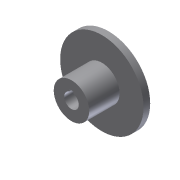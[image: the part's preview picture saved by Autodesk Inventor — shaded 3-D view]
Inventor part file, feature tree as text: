
AUTODESK INVENTOR PART (.ipt)
format: ipt  version: 2013 (Build 170138000, 138)  size: 94,208 bytes
history: native  units: in
note: dims shown in document units (in); Inventor stores cm internally (conversion verified against a paired STEP export)
features: extrude x3, sketch x3
ambient origin geometry x8: Origin, YZ Plane, XZ Plane, XY Plane, X Axis, Y Axis, Z Axis, Center Point
bodies: Solid1 (feature_tree)
feature tree (6):
  extrude  "Extrusion1"  Depth=0.18in TaperAngle=0.0deg
  extrude  "Extrusion2"  Depth=0.82in TaperAngle=0.0deg
  extrude  "Extrusion3"  Depth=0.0984in
  sketch  "Sketch1"  dims[d0=2.25in d1=0.18in d2=0.0in]
  sketch  "Sketch2"  dims[d3=0.958in d4=0.82in d5=0.0in]
  sketch  "Sketch3"  dims[d6=0.3937in d7=0.0984in d8=0.0984in d9=0.82in d10=0.0in]
